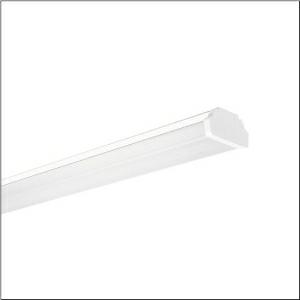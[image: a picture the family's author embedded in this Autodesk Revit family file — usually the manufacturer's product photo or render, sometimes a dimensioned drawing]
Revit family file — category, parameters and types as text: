
# Revit family: dus_r__31_gen_2_53bd812mv485c2_f4cc
name_source: partatom
category: Lighting Fixtures
units: mm (PartAtom-declared; Revit-internal decimal feet)

## family parameters
Cut with Voids When Loaded = No
Host = Face
Light Source = No
Part Type = Normal
Room Calculation Point = No
Round Connector Dimension = Use Diameter
Shared = No

## types (1)
- --- (1 x LED, 8950 lm, 48.2 W, 4000K)
    Apparent Load = 48 VA
    CIE Flux Codes = 47 80 95 93 100
    Color Rendering = 80
    Color Temperature = 4000K
    Default Elevation = 1800 mm
    Description = DUS® 31 Gen.2, luminaire insert, of sheet steel, coil coated, white, length: 1.535mm, width: 81mm, height: 90mm, 5x system unit, system units: 307mm, LED rated luminous flux: 8.950lm, light colour: 840, control gear: ON/OFF Multilumen, control gear: ECG, with plug, 3-pole, with phase selection, mains connection: 220..240V, AC, 50/60Hz, rated input power: 48W, through-wiring accessed according to module size, primary optical cover: cover, of PMMA, light emission: direct distribution, primary light characteristic: symmetric, protection rating (complete): IP20, protection rating (LED compartment): IP50, insulation class (complete): insulation class I (protective earthing), certification: CE, ENEC, VDE, UKCA, impact resistance: IK03, permissible ambient temperature for indoor applications: -35..+50°C, corresponds to IFS (International Featured Standards) requirements for safety and quality in the food industry, reducing of maximum allowable ambient temperature of 5°C with ceiling mounting, packaging unit: 1 piece
    Height = 95 mm
    Lamp = 1 x LED
    Lamp Light Flux = 8950 lm
    Lamp Power = 48.2 W
    Lamp count = 1
    Length = 1535 mm
    Luminous efficacy = 186 lm/W
    Manufacturer = Siteco
    ModVariant = No
    Model = 53BD812MV485C2
    Mounting Place = Ceiling
    Mounting Type = Pendant
    Number of Poles = 1
    OnlyDefault = Yes
    Power Factor = 1
    Product Name = DUS® 31 Gen.2
    Product group = luminaire insert | ceiling pendant
    ProductGroupID = 902
    Protection Class = Protection class I
    Protection Degree = IP 20
    RLX_Detail_Level = 1
    RLX_Emergency_Light_Flux = 0 lm
    RLX_Emergency_Type = 0
    RLX_Emergency_Type_DB = No
    RlxData = <blob elided: 29781 chars, md5=3715b8a4>
    Socket = socket
    Standby Power = 0 W
    System Light Flux = 8950 lm
    System Power = 48 W
    Type Comments = factory setting: luminous flux: 100 % | (A | C | E) | 112 mA
    Type Image = l_1319596.jpg
    URL = http://relux.com
    VarID = @adj_054249
    Voltage = 0 V
    Weight = 0.00 kg
    Width = 81 mm

## geometry (parser evidence)
native form markers: Blend x4, Sweep x13
no freeform markers — native parametric forms only
